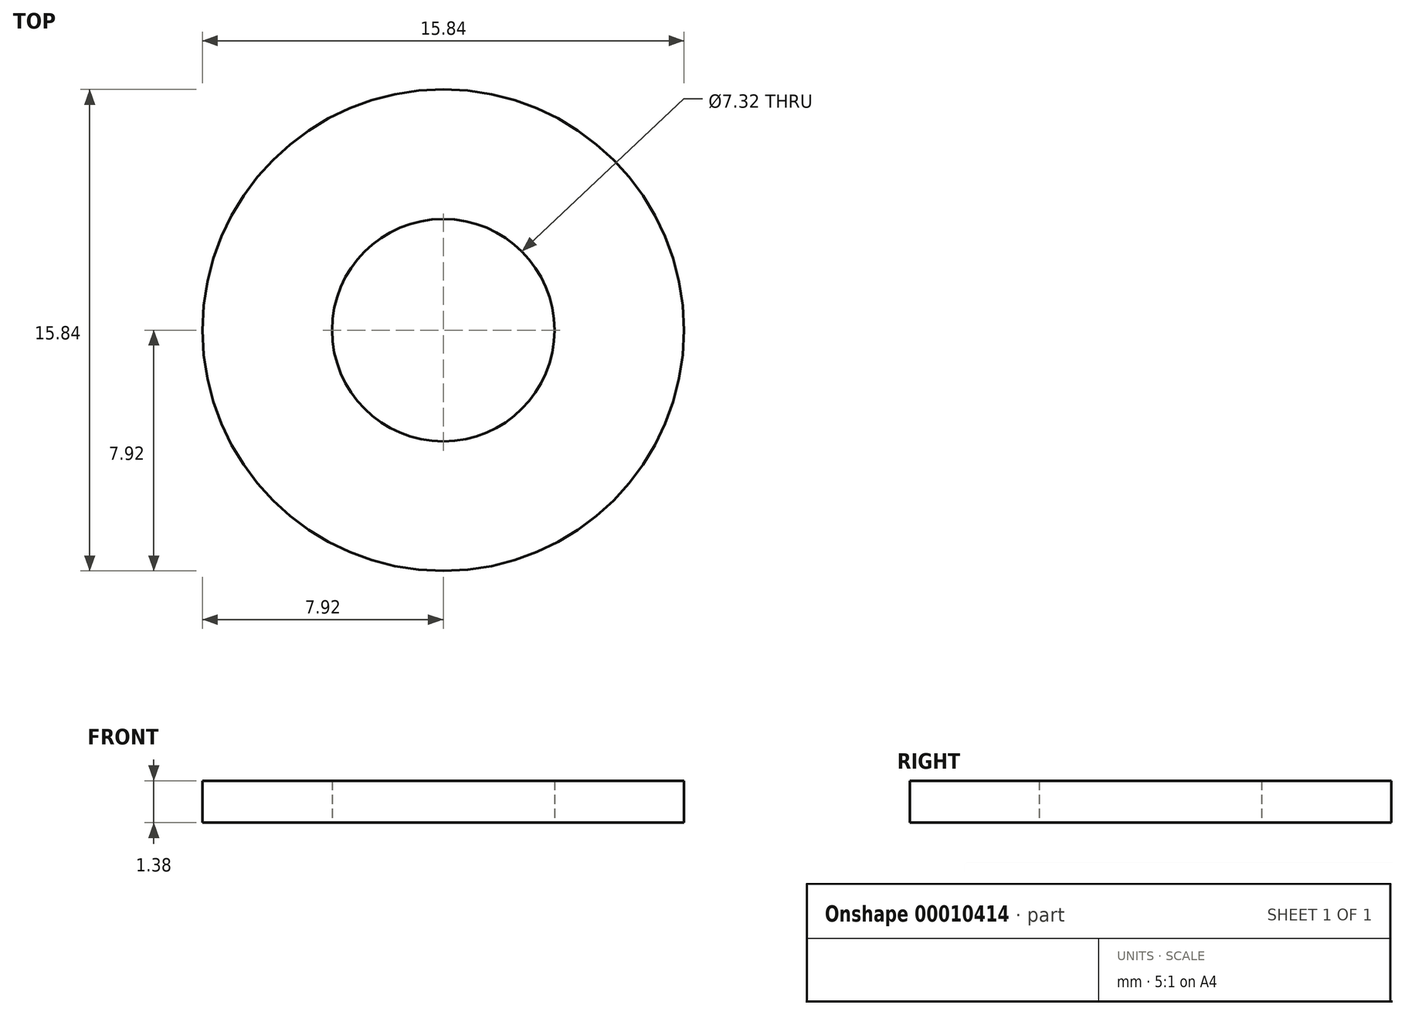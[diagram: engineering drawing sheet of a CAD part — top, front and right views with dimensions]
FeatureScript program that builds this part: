
annotation { "Feature Type Name" : "Feature", "Feature Type Description" : "" }
export const myFeature = defineFeature(function(context is Context, id is Id, definition is map)
    precondition{}
    {
        {
            var Q0;
            Q0=qCreatedBy(makeId("Top.planeOp"),FACE);
            var sketch = newSketch(context, id + "F0", { "sketchPlane" : qUnion([Q0])});
            skCircle(sketch, "E0", {"center": v(0, 0) * mm, "radius": 3.66 * mm});
            skCircle(sketch, "E1", {"center": v(0, 0) * mm, "radius": 7.92 * mm});
            skSolve(sketch);
        }
        {
            var Q0;
            Q0 = qSketchRegion(id + "F0", true);
            extrude(context, id + "F1", {"entities" : qUnion([Q0]), "endBound" : BoundingType.SYMMETRIC, "depth" : 1.37 * mm});
        }
    });
